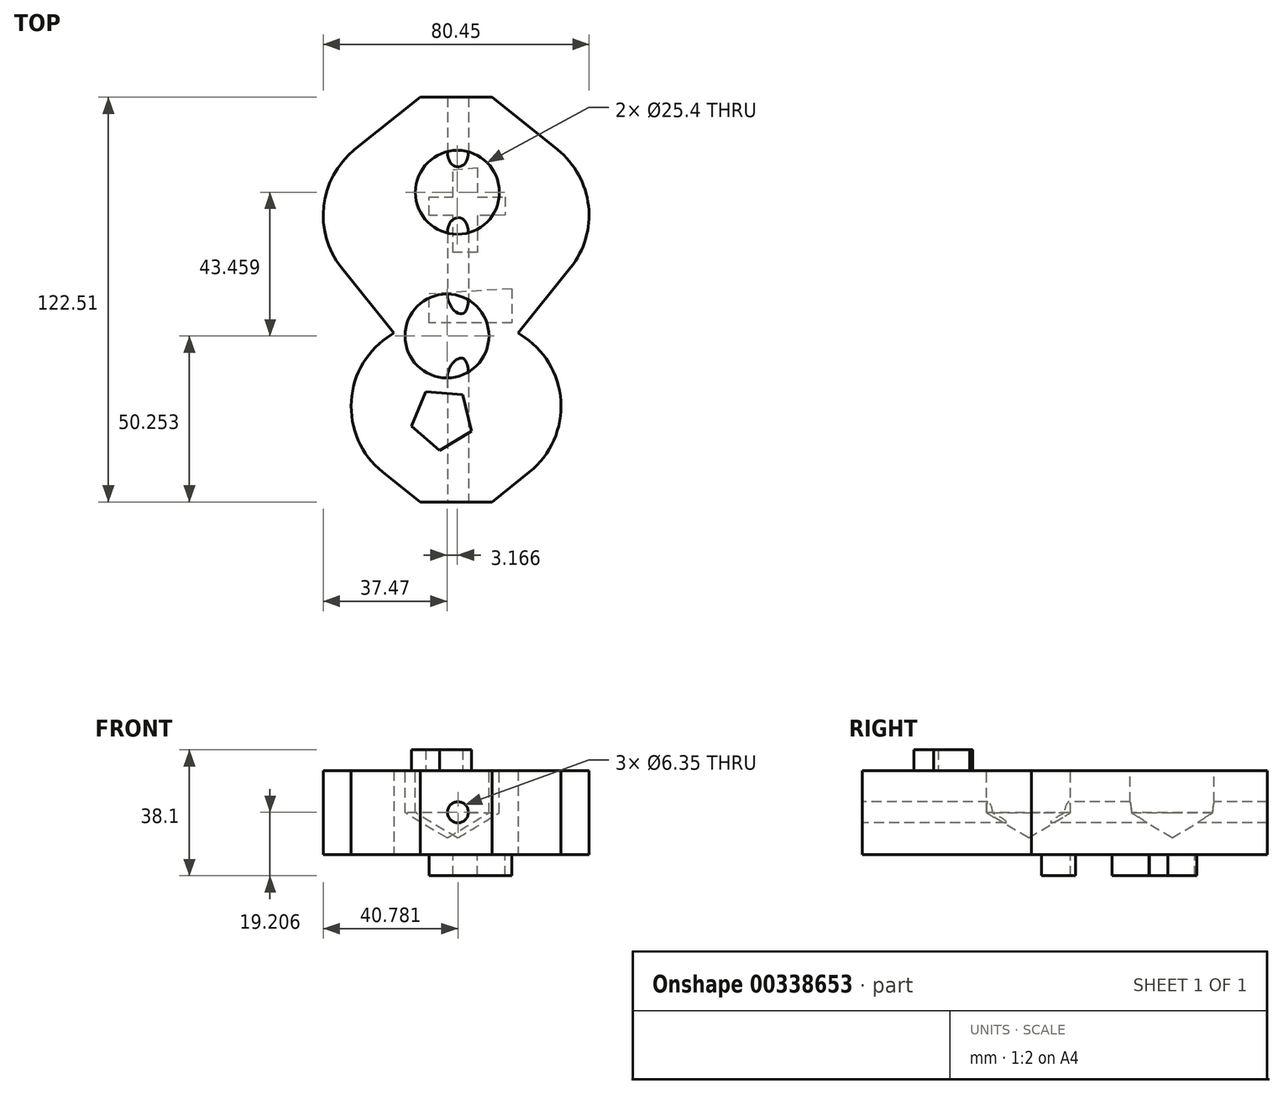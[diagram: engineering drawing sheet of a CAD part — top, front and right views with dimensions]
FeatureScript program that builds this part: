
annotation { "Feature Type Name" : "Feature", "Feature Type Description" : "" }
export const myFeature = defineFeature(function(context is Context, id is Id, definition is map)
    precondition{}
    {
        {
            var Q0;
            Q0=qCreatedBy(makeId("Top.planeOp"),FACE);
            var sketch = newSketch(context, id + "F0", { "sketchPlane" : qUnion([Q0])});
            skLineSegment(sketch, "E0", {"start": v(-17.32, 46.93) * mm, "end": v(-37.16, 31.03) * mm});
            skLineSegment(sketch, "E1", {"start": v(-41.1, -4.67) * mm, "end": v(-25.23, -24.48) * mm});
            skLineSegment(sketch, "E2", {"start": v(-25.23, -24.48) * mm, "end": v(-26, -24.95) * mm});
            skLineSegment(sketch, "E3", {"start": v(-28.69, -66.47) * mm, "end": v(-17.32, -75.58) * mm});
            skLineSegment(sketch, "E4", {"start": v(-17.32, 46.93) * mm, "end": v(4.4, 46.93) * mm});
            skLineSegment(sketch, "E5", {"start": v(4.4, 46.93) * mm, "end": v(24.25, 31.03) * mm});
            skLineSegment(sketch, "E6", {"start": v(28.19, -4.67) * mm, "end": v(12.31, -24.48) * mm});
            skLineSegment(sketch, "E7", {"start": v(12.31, -24.48) * mm, "end": v(13.1, -24.95) * mm});
            skLineSegment(sketch, "E8", {"start": v(15.78, -66.47) * mm, "end": v(4.4, -75.58) * mm});
            skLineSegment(sketch, "E9", {"start": v(4.4, -75.58) * mm, "end": v(-17.32, -75.58) * mm});
            skPoint(sketch, "E10.visualSharp", {"position": v(-56.98, 15.15) * mm});
            skArc(sketch, "E10.filletArc", {"start": v(-37.16, 31.03) * mm, "mid": v(-46.53, 14) * mm, "end": v(-41.1, -4.67) * mm});
            skPoint(sketch, "E11.visualSharp", {"position": v(44.07, 15.15) * mm});
            skArc(sketch, "E11.filletArc", {"start": v(28.19, -4.67) * mm, "mid": v(33.61, 14) * mm, "end": v(24.25, 31.03) * mm});
            skPoint(sketch, "E12.visualSharp", {"position": v(44.07, -43.8) * mm});
            skArc(sketch, "E12.filletArc", {"start": v(15.78, -66.47) * mm, "mid": v(25.24, -45.01) * mm, "end": v(13.1, -24.95) * mm});
            skPoint(sketch, "E13.visualSharp", {"position": v(-56.98, -43.8) * mm});
            skArc(sketch, "E13.filletArc", {"start": v(-26, -24.95) * mm, "mid": v(-38.15, -45.01) * mm, "end": v(-28.69, -66.47) * mm});
            skSolve(sketch);
        }
        {
            var Q0;
            Q0=makeQuery(id+"F0.imprint","IMPRINT",FACE,{"disambiguationData":[TD([[makeQuery(id+"F0.imprint","IMPRINT",EDGE,{"derivedFrom":sQuery(id+"F0.wireOp",EDGE,"E0")}),1.0]])]});
            extrude(context, id + "F1", {"entities" : qUnion([Q0]), "depth" : 25.4 * mm});
        }
        {
            var Q0;
            Q0=makeQuery(id+"F1.opExtrude","CAP_FACE",FACE,{"disambiguationData":[OSD([sQuery(id+"F0.wireOp",EDGE,"E0"),sQuery(id+"F0.wireOp",EDGE,"E1"),sQuery(id+"F0.wireOp",EDGE,"E2"),sQuery(id+"F0.wireOp",EDGE,"E3"),sQuery(id+"F0.wireOp",EDGE,"E4"),sQuery(id+"F0.wireOp",EDGE,"E5"),sQuery(id+"F0.wireOp",EDGE,"E6"),sQuery(id+"F0.wireOp",EDGE,"E7"),sQuery(id+"F0.wireOp",EDGE,"E8"),sQuery(id+"F0.wireOp",EDGE,"E9"),sQuery(id+"F0.wireOp",EDGE,"E10.filletArc"),sQuery(id+"F0.wireOp",EDGE,"E11.filletArc"),sQuery(id+"F0.wireOp",EDGE,"E12.filletArc"),sQuery(id+"F0.wireOp",EDGE,"E13.filletArc")])],"isStart":false});
            var sketch = newSketch(context, id + "F2", { "sketchPlane" : qUnion([Q0])});
            skCircle(sketch, "E14", {"center": v(-6.04, 18.13) * mm, "radius": 12.72 * mm});
            skCircle(sketch, "E15", {"center": v(-9.2, -25.33) * mm, "radius": 12.72 * mm});
            skSolve(sketch);
        }
        {
            var Q0;
            Q0=sQuery(id+"F2.wireOp",VERTEX,"E14.center");
            var Q1;
            Q1=sQuery(id+"F2.wireOp",VERTEX,"E15.center");
            var Q2;
            Q2=makeQuery(id+"F1.opExtrude","SWEPT_BODY",BODY,{"disambiguationData":[OSD([sQuery(id+"F0.wireOp",EDGE,"E0"),sQuery(id+"F0.wireOp",EDGE,"E1"),sQuery(id+"F0.wireOp",EDGE,"E2"),sQuery(id+"F0.wireOp",EDGE,"E3"),sQuery(id+"F0.wireOp",EDGE,"E4"),sQuery(id+"F0.wireOp",EDGE,"E5"),sQuery(id+"F0.wireOp",EDGE,"E6"),sQuery(id+"F0.wireOp",EDGE,"E7"),sQuery(id+"F0.wireOp",EDGE,"E8"),sQuery(id+"F0.wireOp",EDGE,"E9"),sQuery(id+"F0.wireOp",EDGE,"E10.filletArc"),sQuery(id+"F0.wireOp",EDGE,"E11.filletArc"),sQuery(id+"F0.wireOp",EDGE,"E12.filletArc"),sQuery(id+"F0.wireOp",EDGE,"E13.filletArc")])]});
            hole(context, id + "F3", {"style" : HoleStyle.SIMPLE, "endStyle" : HoleEndStyle.BLIND, "holeDiameter" : 25.4 * mm, "holeDepth" : 12.7 * mm, "tappedDepth" : 12.7 * mm, "tapClearance" : 3, "locations" : qUnion([Q0, Q1]), "scope" : qUnion([Q2])});
        }
        {
            var Q0;
            Q0=makeQuery(id+"F1.opExtrude","CAP_FACE",FACE,{"disambiguationData":[OSD([sQuery(id+"F0.wireOp",EDGE,"E0"),sQuery(id+"F0.wireOp",EDGE,"E1"),sQuery(id+"F0.wireOp",EDGE,"E2"),sQuery(id+"F0.wireOp",EDGE,"E3"),sQuery(id+"F0.wireOp",EDGE,"E4"),sQuery(id+"F0.wireOp",EDGE,"E5"),sQuery(id+"F0.wireOp",EDGE,"E6"),sQuery(id+"F0.wireOp",EDGE,"E7"),sQuery(id+"F0.wireOp",EDGE,"E8"),sQuery(id+"F0.wireOp",EDGE,"E9"),sQuery(id+"F0.wireOp",EDGE,"E10.filletArc"),sQuery(id+"F0.wireOp",EDGE,"E11.filletArc"),sQuery(id+"F0.wireOp",EDGE,"E12.filletArc"),sQuery(id+"F0.wireOp",EDGE,"E13.filletArc")])],"isStart":false});
            var sketch = newSketch(context, id + "F4", { "sketchPlane" : qUnion([Q0])});
            skCircle(sketch, "E16.cCircle", {"center": v(-10.65, -50.4) * mm, "radius": 7.75 * mm, "construction": true});
            skLineSegment(sketch, "E16.0", {"start": v(-1.8, -54.09) * mm, "end": v(-11.43, -59.95) * mm});
            skLineSegment(sketch, "E16.1", {"start": v(-11.43, -59.95) * mm, "end": v(-19.98, -52.6) * mm});
            skLineSegment(sketch, "E16.2", {"start": v(-19.98, -52.6) * mm, "end": v(-15.63, -42.2) * mm});
            skLineSegment(sketch, "E16.3", {"start": v(-15.63, -42.2) * mm, "end": v(-4.4, -43.13) * mm});
            skLineSegment(sketch, "E16.4", {"start": v(-4.4, -43.13) * mm, "end": v(-1.8, -54.09) * mm});
            skPoint(sketch, "E16.0.midPoint", {"position": v(-6.62, -57.02) * mm});
            skSolve(sketch);
        }
        {
            var Q0;
            Q0=makeQuery(id+"F4.imprint","IMPRINT",FACE,{"disambiguationData":[TD([[makeQuery(id+"F4.imprint","IMPRINT",EDGE,{"derivedFrom":sQuery(id+"F4.wireOp",EDGE,"E16.0")}),-1.0]])]});
            extrude(context, id + "F5", {"entities" : qUnion([Q0]), "operationType" : NewBodyOperationType.ADD, "depth" : 6.35 * mm});
        }
        {
            var Q0;
            Q0=makeQuery(id+"F1.opExtrude","SWEPT_FACE",FACE,{"disambiguationData":[OSD([sQuery(id+"F0.wireOp",EDGE,"E9")])]});
            var sketch = newSketch(context, id + "F6", { "sketchPlane" : qUnion([Q0])});
            skCircle(sketch, "E17", {"center": v(-5.9, 12.86) * mm, "radius": 5.45 * mm});
            skSolve(sketch);
        }
        {
            var Q0;
            Q0=sQuery(id+"F6.wireOp",VERTEX,"E17.center");
            var Q1;
            Q1=makeQuery(id+"F1.opExtrude","SWEPT_BODY",BODY,{"disambiguationData":[OSD([sQuery(id+"F0.wireOp",EDGE,"E0"),sQuery(id+"F0.wireOp",EDGE,"E1"),sQuery(id+"F0.wireOp",EDGE,"E2"),sQuery(id+"F0.wireOp",EDGE,"E3"),sQuery(id+"F0.wireOp",EDGE,"E4"),sQuery(id+"F0.wireOp",EDGE,"E5"),sQuery(id+"F0.wireOp",EDGE,"E6"),sQuery(id+"F0.wireOp",EDGE,"E7"),sQuery(id+"F0.wireOp",EDGE,"E8"),sQuery(id+"F0.wireOp",EDGE,"E9"),sQuery(id+"F0.wireOp",EDGE,"E10.filletArc"),sQuery(id+"F0.wireOp",EDGE,"E11.filletArc"),sQuery(id+"F0.wireOp",EDGE,"E12.filletArc"),sQuery(id+"F0.wireOp",EDGE,"E13.filletArc")])]});
            hole(context, id + "F7", {"style" : HoleStyle.SIMPLE, "endStyle" : HoleEndStyle.BLIND, "holeDiameter" : 6.35 * mm, "holeDepth" : 254 * mm, "isTappedThrough" : true, "tappedDepth" : 12.7 * mm, "tapClearance" : 3, "locations" : qUnion([Q0]), "scope" : qUnion([Q1])});
        }
        {
            var Q0;
            Q0=makeQuery(id+"F1.opExtrude","CAP_FACE",FACE,{"disambiguationData":[OSD([sQuery(id+"F0.wireOp",EDGE,"E0"),sQuery(id+"F0.wireOp",EDGE,"E1"),sQuery(id+"F0.wireOp",EDGE,"E2"),sQuery(id+"F0.wireOp",EDGE,"E3"),sQuery(id+"F0.wireOp",EDGE,"E4"),sQuery(id+"F0.wireOp",EDGE,"E5"),sQuery(id+"F0.wireOp",EDGE,"E6"),sQuery(id+"F0.wireOp",EDGE,"E7"),sQuery(id+"F0.wireOp",EDGE,"E8"),sQuery(id+"F0.wireOp",EDGE,"E9"),sQuery(id+"F0.wireOp",EDGE,"E10.filletArc"),sQuery(id+"F0.wireOp",EDGE,"E11.filletArc"),sQuery(id+"F0.wireOp",EDGE,"E12.filletArc"),sQuery(id+"F0.wireOp",EDGE,"E13.filletArc")])],"isStart":true});
            var sketch = newSketch(context, id + "F8", { "sketchPlane" : qUnion([Q0])});
            skLineSegment(sketch, "E18", {"start": v(0, -25.56) * mm, "end": v(0, -16.79) * mm});
            skLineSegment(sketch, "E19", {"start": v(0, -16.79) * mm, "end": v(8.32, -16.79) * mm});
            skLineSegment(sketch, "E20", {"start": v(8.32, -16.79) * mm, "end": v(8.37, -11.21) * mm});
            skLineSegment(sketch, "E21", {"start": v(8.37, -11.21) * mm, "end": v(0, -11.14) * mm});
            skLineSegment(sketch, "E22", {"start": v(0, -11.14) * mm, "end": v(0, 0) * mm});
            skLineSegment(sketch, "E23", {"start": v(0, 0) * mm, "end": v(-7.41, 0) * mm});
            skLineSegment(sketch, "E24", {"start": v(-7.41, 0) * mm, "end": v(-7.41, -11.14) * mm});
            skLineSegment(sketch, "E25", {"start": v(-7.41, -11.14) * mm, "end": v(-14.67, -11.14) * mm});
            skLineSegment(sketch, "E26", {"start": v(-14.67, -11.14) * mm, "end": v(-14.67, -16.79) * mm});
            skLineSegment(sketch, "E27", {"start": v(-14.67, -16.79) * mm, "end": v(-7.41, -16.79) * mm});
            skLineSegment(sketch, "E28", {"start": v(-7.41, -16.79) * mm, "end": v(-7.41, -24.96) * mm});
            skLineSegment(sketch, "E29", {"start": v(-7.41, -24.96) * mm, "end": v(0, -25.56) * mm});
            skSolve(sketch);
        }
        {
            var Q0;
            Q0=makeQuery(id+"F8.imprint","IMPRINT",FACE,{"disambiguationData":[TD([[makeQuery(id+"F8.imprint","IMPRINT",EDGE,{"derivedFrom":sQuery(id+"F8.wireOp",EDGE,"E18")}),1.0]])]});
            extrude(context, id + "F9", {"entities" : qUnion([Q0]), "operationType" : NewBodyOperationType.ADD, "depth" : 6.35 * mm});
        }
        {
            var Q0;
            Q0=makeQuery(id+"F1.opExtrude","CAP_FACE",FACE,{"disambiguationData":[OSD([sQuery(id+"F0.wireOp",EDGE,"E0"),sQuery(id+"F0.wireOp",EDGE,"E1"),sQuery(id+"F0.wireOp",EDGE,"E2"),sQuery(id+"F0.wireOp",EDGE,"E3"),sQuery(id+"F0.wireOp",EDGE,"E4"),sQuery(id+"F0.wireOp",EDGE,"E5"),sQuery(id+"F0.wireOp",EDGE,"E6"),sQuery(id+"F0.wireOp",EDGE,"E7"),sQuery(id+"F0.wireOp",EDGE,"E8"),sQuery(id+"F0.wireOp",EDGE,"E9"),sQuery(id+"F0.wireOp",EDGE,"E10.filletArc"),sQuery(id+"F0.wireOp",EDGE,"E11.filletArc"),sQuery(id+"F0.wireOp",EDGE,"E12.filletArc"),sQuery(id+"F0.wireOp",EDGE,"E13.filletArc")])],"isStart":true});
            var sketch = newSketch(context, id + "F10", { "sketchPlane" : qUnion([Q0])});
            skLineSegment(sketch, "E30", {"start": v(10.44, 11.04) * mm, "end": v(10.44, 21.33) * mm});
            skLineSegment(sketch, "E31", {"start": v(10.44, 21.33) * mm, "end": v(-14.67, 21.33) * mm});
            skLineSegment(sketch, "E32", {"start": v(-14.67, 21.33) * mm, "end": v(-14.67, 12.58) * mm});
            skLineSegment(sketch, "E33", {"start": v(10.44, 11.04) * mm, "end": v(-14.67, 12.58) * mm});
            skSolve(sketch);
        }
        {
            var Q0;
            Q0=makeQuery(id+"F10.imprint","IMPRINT",FACE,{"disambiguationData":[TD([[makeQuery(id+"F10.imprint","IMPRINT",EDGE,{"derivedFrom":sQuery(id+"F10.wireOp",EDGE,"E30")}),1.0]])]});
            extrude(context, id + "F11", {"entities" : qUnion([Q0]), "operationType" : NewBodyOperationType.ADD, "depth" : 6.35 * mm});
        }
    });
